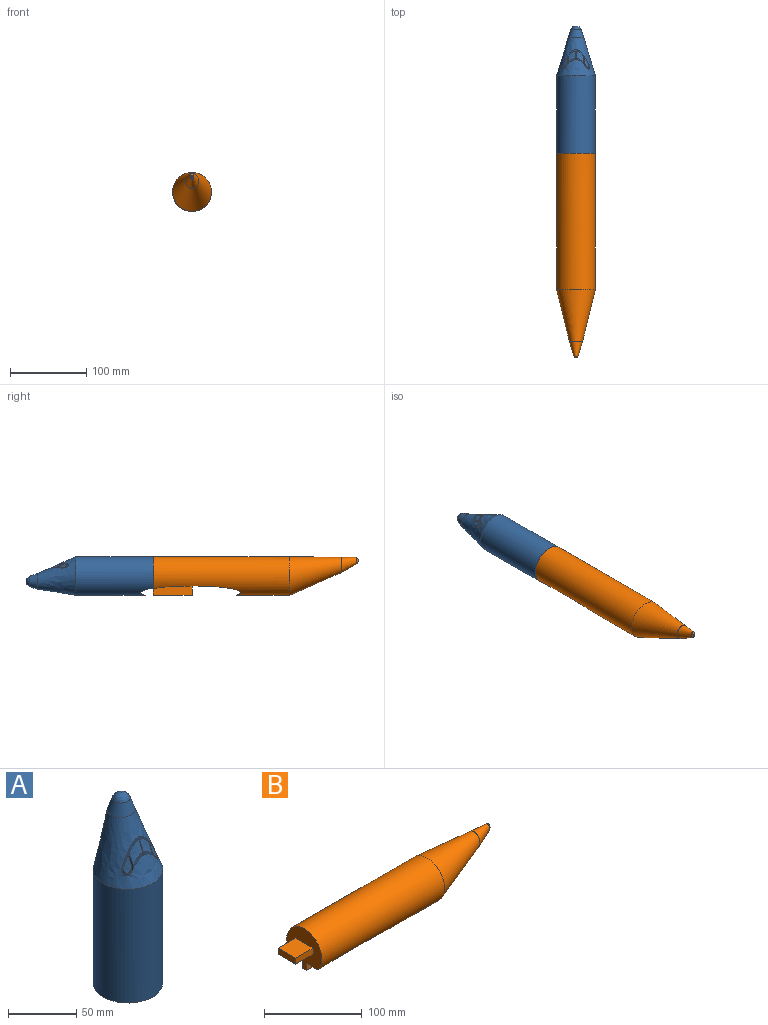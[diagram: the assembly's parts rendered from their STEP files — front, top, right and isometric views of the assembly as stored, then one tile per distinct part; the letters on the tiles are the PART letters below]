
ASSEMBLY  parts=2 mates=1
PART A: 41 faces, bbox 54x54x169.8 mm
  f0: plane 50.8x41.14mm, normal (0,0,-1), area 1564.8mm2, adj f1,f35,f36,f37,f38,f40
  f1: cylinder r=25.4mm len=101.6mm, axis (0,0,-1), area 15626.8mm2, adj f0,f2,f40
  f2: bspline ~50.77x50.75mm, area 5387.9mm2, adj f1,f3,f13,f14,f15,f16,f17,f26
  f3: bspline ~20.58x20.58mm, area 576.6mm2, adj f2,f5
  f4: plane 0.27x0.27mm, normal (0,0,1), area 0.1mm2, adj f5
  f5: bspline ~13.18x13.17mm, area 203.4mm2, adj f3,f4
  f6: plane 19.74x4.24mm, normal (1,0,0), area 63.2mm2, adj f7,f29,f30,f34
  f7: plane 19.3x11.42mm, normal (0,-1,0), area 135.3mm2, adj f6,f8,f30,f34
  f8: plane 26.27x4.16mm, normal (-1,0,0), area 88.1mm2, adj f7,f29,f30,f34
  f9: plane 9.92x2.12mm, normal (0,-1,0), area 17.3mm2, adj f10,f25,f30,f33
  f10: plane 18.03x4.25mm, normal (-1,0,0), area 56.7mm2, adj f9,f11,f30,f33
  f11: plane 17.86x5.84mm, normal (0,1,0), area 76mm2, adj f10,f12,f30,f33
  f12: plane 7.61x0.28mm, normal (1,0,0), area 2mm2, adj f11,f25,f30,f33
  f13: cylinder r=5.08mm len=5.81mm, axis (0,0,1), area 30.4mm2, adj f2,f14,f26,f30
  f14: plane 6.83x0.75mm, normal (-1,0,0), area 4.7mm2, adj f2,f13,f15,f30
  f15: plane 35.22x28.28mm, normal (0,-1,0), area 739.1mm2, adj f2,f14,f16,f30
  f16: plane 7.82x0.75mm, normal (1,0,0), area 5.4mm2, adj f2,f15,f17,f30
  f17: cylinder r=5.08mm len=6.7mm, axis (0,0,1), area 52.4mm2, adj f2,f16,f26,f30
  f18: plane 17.57x5.33mm, normal (0,1,0), area 70mm2, adj f19,f27,f30,f32
  f19: plane 17.66x4.18mm, normal (1,0,0), area 55.6mm2, adj f18,f20,f30,f32
  f20: plane 9.63x1.57mm, normal (0,-1,0), area 13mm2, adj f19,f21,f30,f32
  f21: cylinder r=3.81mm len=7.8mm, axis (0,0,1), area 45.9mm2, adj f20,f27,f30,f32
  f22: plane 29.44x13.04mm, normal (0,1,0), area 235.4mm2, adj f23,f28,f30,f31
  f23: plane 26.29x4.15mm, normal (1,0,0), area 88.2mm2, adj f22,f24,f30,f31
  f24: plane 19.79x12.66mm, normal (0,-1,0), area 147.8mm2, adj f23,f28,f30,f31
  f25: cylinder r=3.81mm len=7.18mm, axis (0,0,1), area 42.6mm2, adj f9,f12,f30,f33
  f26: plane 25.06x15.08mm, normal (0,1,0), area 301.7mm2, adj f2,f13,f17,f30
  f27: plane 8.24x0.28mm, normal (-1,0,0), area 2.2mm2, adj f18,f21,f30,f32
  f28: plane 19.52x4.16mm, normal (-1,0,0), area 62.7mm2, adj f22,f24,f30,f31
  f29: plane 28.84x11.71mm, normal (0,1,0), area 216mm2, adj f6,f8,f30,f34
  f30: plane 35.22x5.82mm, normal (0,0,1), area 77.3mm2, adj f6,f7,f8,f9,f10,f11,f12,f13
  f31: bspline ~50.29x26.19mm, area 99.2mm2, adj f22,f23,f24,f28
  f32: bspline ~50.29x28.52mm, area 49mm2, adj f18,f19,f20,f21,f27
  f33: bspline ~50.29x21.7mm, area 54.5mm2, adj f9,f10,f11,f12,f25
  f34: bspline ~50.29x23.79mm, area 91.7mm2, adj f6,f7,f8,f29
  f35: plane 25.4x25.4mm, normal (0,1,0), area 645.2mm2, adj f0,f36,f38,f39
  f36: plane 25.4x7.62mm, normal (1,0,0), area 193.5mm2, adj f0,f35,f37,f39
  f37: plane 25.4x25.4mm, normal (0,-1,0), area 645.2mm2, adj f0,f36,f38,f39
  f38: plane 25.4x7.62mm, normal (-1,0,0), area 193.5mm2, adj f0,f35,f37,f39
  f39: plane 25.4x7.62mm, normal (0,0,-1), area 193.5mm2, adj f35,f36,f37,f38
  f40: extruded ~39.87x16.47mm, area 761.5mm2, adj f0,f1
PART B: 19 faces, bbox 293.1x50.8x50.8 mm
  f0: cylinder r=25.4mm len=177.8mm, axis (-1,0,0), area 22838.5mm2, adj f1,f7,f14
  f1: plane 50.8x50.8mm, normal (-1,0,0), area 1635.8mm2, adj f0,f2,f3,f4,f5,f14,f15,f17
  f2: plane 25.4x7.62mm, normal (0,1,0), area 193.5mm2, adj f1,f3,f5,f6
  f3: plane 25.4x25.4mm, normal (0,0,-1), area 645.2mm2, adj f1,f2,f4,f6
  f4: plane 25.4x7.62mm, normal (0,-1,0), area 193.5mm2, adj f1,f3,f5,f6
  f5: plane 25.4x25.4mm, normal (0,0,1), area 645.2mm2, adj f1,f2,f4,f6
  f6: plane 25.4x7.62mm, normal (-1,0,0), area 193.5mm2, adj f2,f3,f4,f5
  f7: bspline ~67.82x50.8mm, area 7659.3mm2, adj f0,f9
  f8: plane 2.41x0.32mm, normal (1,0,0), area 0.5mm2, adj f11,f12
  f9: bspline ~22.1x19.79mm, area 854.3mm2, adj f7,f10,f11,f12,f13
  f10: bspline ~3.98x3.09mm, area 7.9mm2, adj f9,f11,f12
  f11: bspline ~6.03x2.77mm, area 12.8mm2, adj f8,f9,f10,f13
  f12: bspline ~5.91x2.75mm, area 12.8mm2, adj f8,f9,f10,f13
  f13: bspline ~3.6x2.81mm, area 5.3mm2, adj f9,f11,f12
  f14: extruded ~114.27x43.85mm, area 4680.1mm2, adj f0,f1,f15,f16,f17
  f15: plane 50.8x12.58mm, normal (0,-1,0), area 584.5mm2, adj f1,f14,f16,f18
  f16: plane 12.58x5.08mm, normal (1,0,0), area 63.9mm2, adj f14,f15,f17,f18
  f17: plane 50.8x12.58mm, normal (0,1,0), area 584.5mm2, adj f1,f14,f16,f18
  f18: plane 50.8x5.08mm, normal (0,0,-1), area 258.1mm2, adj f1,f15,f16,f17
PLACE A rot(axis=(-1,0,0),90deg) t=(0,81.51,19.73)mm
PLACE B rot(axis=(0,0,-1),90deg) t=(0,81.51,19.73)mm
MATE slider B.f6 <-> A.f39  axis (0,1,0) through (0,106.91,23.54)mm
